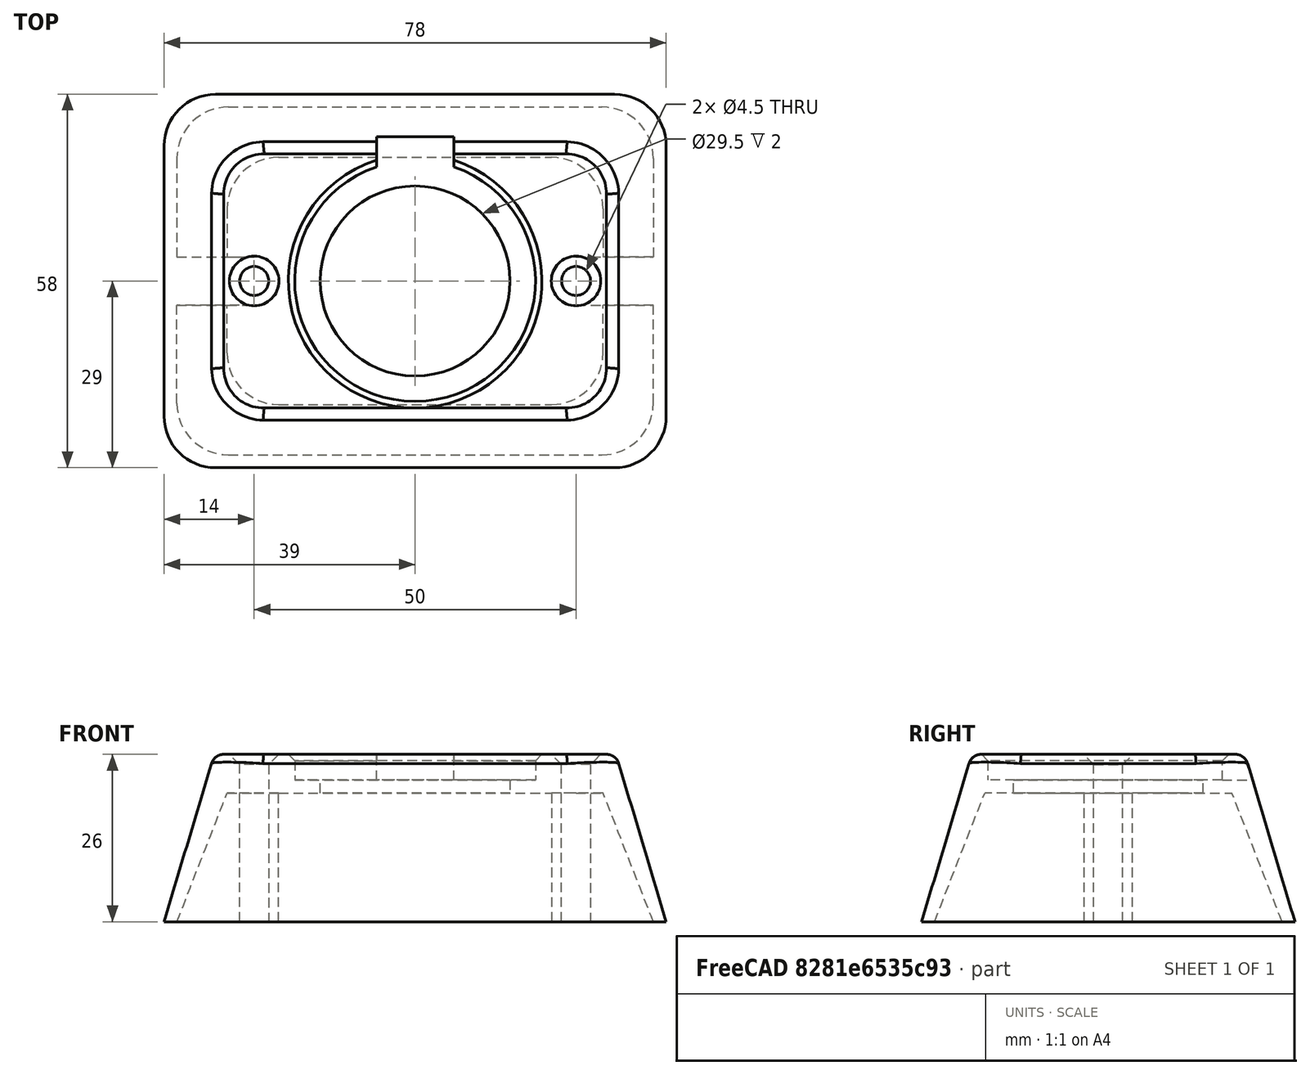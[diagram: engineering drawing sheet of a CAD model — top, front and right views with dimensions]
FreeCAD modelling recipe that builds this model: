
FCSTD DOCUMENT  (FreeCAD 0.20R29410 (Git))
Label: usb_spacer
License: All rights reserved
LicenseURL: http://en.wikipedia.org/wiki/All_rights_reserved
objects: Sketcher::SketchObject×6, PartDesign::Pocket×2, PartDesign::Chamfer×2, Spreadsheet::Sheet×1, PartDesign::AdditiveLoft×1, PartDesign::SubtractiveLoft×1, PartDesign::Fillet×1, PartDesign::Body×1, App::Part×1, Mesh::Feature×1
note: 21 computed .brp shape members not serialized (recipe doc carries the construction recipe); baked Part::Feature solids carry a one-line shape summary decoded from their .brp

FEATURE [Sketcher::SketchObject] Sketch  label="Sketch.Bottom"
  FullyConstrained = true
  MapMode = 5
  Support = -> [XY_Plane001]
  expr: Constraints[16] = <<Parameters>>.large_radius
  expr: Constraints[17] = <<Parameters>>.bottom_width
  expr: Constraints[3] = <<Parameters>>.bottom_length
  sketch-geometry (8):
    g0: LineSegment StartX=39 StartY=21 StartZ=0 EndX=39 EndY=-21 EndZ=0
    g1: LineSegment StartX=-39 StartY=-21 StartZ=0 EndX=-39 EndY=21 EndZ=0
    g2: ArcOfCircle CenterX=-31 CenterY=21 CenterZ=0 NormalX=0 NormalY=0 NormalZ=1 AngleXU=0 Radius=8 StartAngle=1.5708 EndAngle=3.14159
    g3: ArcOfCircle CenterX=31 CenterY=21 CenterZ=0 NormalX=0 NormalY=0 NormalZ=1 AngleXU=0 Radius=8 StartAngle=2e-16 EndAngle=1.5708
    g4: LineSegment StartX=-31 StartY=29 StartZ=0 EndX=31 EndY=29 EndZ=0
    g5: ArcOfCircle CenterX=-31 CenterY=-21 CenterZ=0 NormalX=0 NormalY=0 NormalZ=1 AngleXU=0 Radius=8 StartAngle=3.14159 EndAngle=4.71239
    g6: ArcOfCircle CenterX=31 CenterY=-21 CenterZ=0 NormalX=0 NormalY=0 NormalZ=1 AngleXU=0 Radius=8 StartAngle=4.71239 EndAngle=6.28319
    g7: LineSegment StartX=-31 StartY=-29 StartZ=0 EndX=31 EndY=-29 EndZ=0
  constraints (18):
    c: Vertical(g1)
    c: Symmetric(g1,g0,g-2)
    c: Symmetric(g0,g0,g-1)
    c: DistanceX(g1,g0) = 78
    c: Horizontal(g4)
    c: Horizontal(g7)
    c: Equal(g4,g7)
    c: Equal(g0,g1)
    c: Tangent(g4,g3) = 1.5708
    c: Tangent(g3,g0) = 1.5708
    c: Tangent(g4,g2) = 1.5708
    c: Tangent(g2,g1) = 1.5708
    c: Tangent(g5,g1) = 1.5708
    c: Tangent(g7,g5) = -1.5708
    c: Tangent(g7,g6) = -1.5708
    c: Tangent(g6,g0) = 1.5708
    c: Radius(g2) = 8
    c: DistanceY(g6,g3) = 58
FEATURE [Spreadsheet::Sheet] Spreadsheet  label="Parameters"
  cells = A1=Bottom; B2=bottom_length; C2(bottom_length)=78; B3=bottom_width; C3(bottom_width)=58; B4=bottom_wall; C4(bottom_wall)=2; A6=Top; B7=top_length; C7(top_length)==C2 - C13 * C18; D7=calc; B8=top_width; C8(top_width)==C3 - C13 * C18; D8=calc; B9=wall_taper_length; C9(wall_taper_length)==C2 - C13 * C18 - 2 * C4; D9=calc; B10=wall_taper_width; C10(wall_taper_width)==C3 - C13 * C18 - 2 * C4; D10=calc; A12=General; B13=height; C13(height)=26; B14=hole_diameter; C14(hole_diameter)=29.5; B15=face_thickness; C15(face)=6; B16=large_radius; C16(large_radius)=8; B17=small_radius; C17(small_radius)=2; B18=taper; C18=0.6; B19=flange_diameter; C19(flange_diameter)=37.4; B20=flange_depth; C20(flange_depth)=4; B21=cover_tab; C21(cover_tab)=12; A23=Screws; B24=screw_hole_diameter; C24(screw_hole_diameter)=4.5; B25=screw_seperation; C25(screw_seperation)=50; B26=post_diameter; C26(post_diameter)==C24 + 3; D26=calc; B27=screw_chamfer; C27(screw_chamfer)=1.6; A29=Switch; B30=switch_hole_diameter; C30(switch_hole_diameter)=6.1; B31=switch_offset; C31(switch_offset)=11
FEATURE [Sketcher::SketchObject] Sketch001  label="Sketch.Top"
  AttachmentOffset = pos=(0,0,26) rot=(0,0,1;0rad)
  FullyConstrained = true
  MapMode = 5
  Placement = pos=(0,0,26) rot=(0,0,1;0rad)
  Support = -> [XY_Plane001]
  expr: .AttachmentOffset.Base.z = <<Parameters>>.height
  expr: Constraints[15] = <<Parameters>>.top_width
  expr: Constraints[2] = <<Parameters>>.top_length
  expr: Constraints[3] = <<Parameters>>.large_radius
  sketch-geometry (8):
    g0: LineSegment StartX=31.2 StartY=13.2 StartZ=0 EndX=31.2 EndY=-13.2 EndZ=0
    g1: LineSegment StartX=-31.2 StartY=-13.2 StartZ=0 EndX=-31.2 EndY=13.2 EndZ=0
    g2: ArcOfCircle CenterX=-23.2 CenterY=-13.2 CenterZ=0 NormalX=0 NormalY=0 NormalZ=1 AngleXU=0 Radius=8 StartAngle=3.14159 EndAngle=4.71239
    g3: ArcOfCircle CenterX=23.2 CenterY=-13.2 CenterZ=0 NormalX=0 NormalY=0 NormalZ=1 AngleXU=0 Radius=8 StartAngle=4.71239 EndAngle=6.28319
    g4: LineSegment StartX=-23.2 StartY=-21.2 StartZ=0 EndX=23.2 EndY=-21.2 EndZ=0
    g5: ArcOfCircle CenterX=-23.2 CenterY=13.2 CenterZ=0 NormalX=0 NormalY=0 NormalZ=1 AngleXU=0 Radius=8 StartAngle=1.5708 EndAngle=3.14159
    g6: ArcOfCircle CenterX=23.2 CenterY=13.2 CenterZ=0 NormalX=0 NormalY=0 NormalZ=1 AngleXU=0 Radius=8 StartAngle=2e-16 EndAngle=1.5708
    g7: LineSegment StartX=-23.2 StartY=21.2 StartZ=0 EndX=23.2 EndY=21.2 EndZ=0
  constraints (16):
    c: Symmetric(g0,g0,g-1)
    c: Symmetric(g1,g0,g-2)
    c: DistanceX(g1,g0) = 62.4
    c: Radius(g5) = 8
    c: Symmetric(g5,g6,g-2)
    c: Tangent(g2,g1) = 1.5708
    c: Tangent(g4,g2) = -1.5708
    c: Tangent(g3,g0) = 1.5708
    c: Tangent(g4,g3) = -1.5708
    c: Tangent(g7,g6) = 1.5708
    c: Tangent(g6,g0) = 1.5708
    c: Tangent(g7,g5) = 1.5708
    c: Tangent(g5,g1) = 1.5708
    c: Symmetric(g2,g3,g-2)
    c: Equal(g4,g7)
    c: DistanceY(g3,g6) = 42.4
FEATURE [PartDesign::AdditiveLoft] AdditiveLoft  label="AdditiveLoft.Main"
  Closed = false
  Profile = -> Sketch
  Ruled = false
  Sections = -> [Sketch001]
FEATURE [Sketcher::SketchObject] Sketch002  label="Sketch.Holes"
  FullyConstrained = true
  MapMode = 5
  Support = -> [XY_Plane001]
  expr: Constraints[1] = <<Parameters>>.hole_diameter
  expr: Constraints[4] = <<Parameters>>.screw_seperation
  expr: Constraints[6] = <<Parameters>>.screw_hole_diameter
  sketch-geometry (3):
    g0: Circle CenterX=0 CenterY=0 CenterZ=0 NormalX=0 NormalY=0 NormalZ=1 AngleXU=0 Radius=14.75
    g1: Circle CenterX=-25 CenterY=0 CenterZ=0 NormalX=0 NormalY=0 NormalZ=1 AngleXU=0 Radius=2.25
    g2: Circle CenterX=25 CenterY=-1.76111e-11 CenterZ=0 NormalX=0 NormalY=0 NormalZ=1 AngleXU=0 Radius=2.25
  constraints (7):
    c: Coincident(g0,g-1)
    c: Diameter(g0) = 29.5
    c: PointOnObject(g1,g-1)
    c: Symmetric(g2,g1,g0)
    c: DistanceX(g1,g2) = 50
    c: Equal(g2,g1)
    c: Diameter(g2) = 4.5
FEATURE [PartDesign::Pocket] Pocket  label="Pocket.Screw"
  BaseFeature = -> AdditiveLoft
  Direction = (0,0,-1)
  Length = 78
  Length2 = 5
  Midplane = true
  Profile = -> Sketch002
  ReferenceAxis = -> Sketch002 [N_Axis]
  Type = 0
  expr: Length = <<Parameters>>.height * 3
FEATURE [Sketcher::SketchObject] Sketch003  label="Sketch.Interior.Bottom"
  FullyConstrained = true
  MapMode = 5
  Support = -> [XY_Plane001]
  expr: Constraints[15] = <<Parameters>>.post_diameter
  expr: Constraints[31] = <<Parameters>>.screw_seperation
  expr: Constraints[39] = <<Parameters>>.bottom_length - <<Parameters>>.bottom_wall * 2
  expr: Constraints[6] = <<Parameters>>.large_radius
  expr: Constraints[7] = <<Parameters>>.bottom_width - <<Parameters>>.bottom_wall * 2
  sketch-geometry (16):
    g0: ArcOfCircle CenterX=-29 CenterY=19 CenterZ=0 NormalX=0 NormalY=0 NormalZ=1 AngleXU=0 Radius=8 StartAngle=1.5708 EndAngle=3.14159
    g1: ArcOfCircle CenterX=29 CenterY=19 CenterZ=0 NormalX=0 NormalY=0 NormalZ=1 AngleXU=0 Radius=8 StartAngle=0 EndAngle=1.5708
    g2: ArcOfCircle CenterX=-29 CenterY=-19 CenterZ=0 NormalX=0 NormalY=0 NormalZ=1 AngleXU=0 Radius=8 StartAngle=3.14159 EndAngle=4.71239
    g3: ArcOfCircle CenterX=29 CenterY=-19 CenterZ=0 NormalX=0 NormalY=0 NormalZ=1 AngleXU=0 Radius=8 StartAngle=4.71239 EndAngle=6.28319
    g4: LineSegment StartX=-29 StartY=27 StartZ=0 EndX=29 EndY=27 EndZ=0
    g5: LineSegment StartX=-29 StartY=-27 StartZ=0 EndX=29 EndY=-27 EndZ=0
    g6: ArcOfCircle CenterX=-25 CenterY=0 CenterZ=0 NormalX=0 NormalY=0 NormalZ=1 AngleXU=0 Radius=3.75 StartAngle=4.71239 EndAngle=7.85398
    g7: LineSegment StartX=-37 StartY=19 StartZ=0 EndX=-37 EndY=3.75 EndZ=0
    g8: LineSegment StartX=-37 StartY=3.75 StartZ=0 EndX=-25 EndY=3.75 EndZ=0
    g9: LineSegment StartX=-25 StartY=-3.75 StartZ=0 EndX=-37 EndY=-3.75 EndZ=0
    g10: LineSegment StartX=-37 StartY=-19 StartZ=0 EndX=-37 EndY=-3.75 EndZ=0
    g11: ArcOfCircle CenterX=25 CenterY=0 CenterZ=0 NormalX=0 NormalY=0 NormalZ=1 AngleXU=0 Radius=3.75 StartAngle=1.5708 EndAngle=4.71239
    g12: LineSegment StartX=37 StartY=19 StartZ=0 EndX=37 EndY=3.75 EndZ=0
    g13: LineSegment StartX=37 StartY=-19 StartZ=0 EndX=37 EndY=-3.75 EndZ=0
    g14: LineSegment StartX=25 StartY=-3.75 StartZ=0 EndX=37 EndY=-3.75 EndZ=0
    g15: LineSegment StartX=25 StartY=3.75 StartZ=0 EndX=37 EndY=3.75 EndZ=0
  constraints (40):
    c: Horizontal(g5)
    c: Equal(g4,g5)
    c: Tangent(g4,g1) = 1.5708
    c: Tangent(g5,g3) = -1.5708
    c: Tangent(g5,g2) = -1.5708
    c: Tangent(g4,g0) = 1.5708
    c: Radius(g0) = 8
    c: DistanceY(g3,g1) = 54
    c: PointOnObject(g6,g-1)
    c: Vertical(g7)
    c: Coincident(g8,g7)
    c: Horizontal(g8)
    c: Horizontal(g9)
    c: Coincident(g10,g9)
    c: Vertical(g10)
    c: Diameter(g6) = 7.5
    c: Equal(g8,g9)
    c: Equal(g7,g10)
    c: Tangent(g8,g6) = 1.5708
    c: Tangent(g9,g6) = 1.5708
    c: Symmetric(g0,g1,g-2)
    c: Vertical(g12)
    c: Vertical(g13)
    c: Coincident(g14,g13)
    c: Horizontal(g14)
    c: Coincident(g15,g12)
    c: Horizontal(g15)
    c: Equal(g8,g15)
    c: Equal(g9,g14)
    c: Equal(g7,g12)
    c: Equal(g10,g13)
    c: DistanceX(g6,g11) = 50
    c: Tangent(g15,g11) = 1.5708
    c: Tangent(g14,g11) = -1.5708
    c: Symmetric(g6,g11,g-2)
    c: Tangent(g13,g3) = -1.5708
    c: Tangent(g12,g1) = 1.5708
    c: Tangent(g10,g2) = 1.5708
    c: Tangent(g7,g0) = -1.5708
    c: DistanceX(g2,g3) = 74
FEATURE [Sketcher::SketchObject] Sketch004  label="Sketch.Interior.Top"
  AttachmentOffset = pos=(0,0,20) rot=(0,0,1;0rad)
  FullyConstrained = true
  MapMode = 5
  Placement = pos=(0,0,20) rot=(0,0,1;0rad)
  Support = -> [XY_Plane001]
  expr: .AttachmentOffset.Base.z = <<Parameters>>.height - <<Parameters>>.face
  expr: Constraints[10] = <<Parameters>>.wall_taper_width
  expr: Constraints[12] = <<Parameters>>.post_diameter
  expr: Constraints[35] = <<Parameters>>.screw_seperation
  expr: Constraints[38] = <<Parameters>>.wall_taper_length
  expr: Constraints[6] = <<Parameters>>.large_radius
  sketch-geometry (16):
    g0: ArcOfCircle CenterX=-21.2 CenterY=11.2 CenterZ=0 NormalX=0 NormalY=0 NormalZ=1 AngleXU=0 Radius=8 StartAngle=1.5708 EndAngle=3.14159
    g1: ArcOfCircle CenterX=-21.2 CenterY=-11.2 CenterZ=0 NormalX=0 NormalY=0 NormalZ=1 AngleXU=0 Radius=8 StartAngle=3.14159 EndAngle=4.71239
    g2: ArcOfCircle CenterX=21.2 CenterY=-11.2 CenterZ=0 NormalX=0 NormalY=0 NormalZ=1 AngleXU=0 Radius=8 StartAngle=4.71239 EndAngle=6.28319
    g3: ArcOfCircle CenterX=21.2 CenterY=11.2 CenterZ=0 NormalX=0 NormalY=0 NormalZ=1 AngleXU=0 Radius=8 StartAngle=0 EndAngle=1.5708
    g4: LineSegment StartX=-21.2 StartY=19.2 StartZ=0 EndX=21.2 EndY=19.2 EndZ=0
    g5: LineSegment StartX=-21.2 StartY=-19.2 StartZ=0 EndX=21.2 EndY=-19.2 EndZ=0
    g6: ArcOfCircle CenterX=-25 CenterY=0 CenterZ=0 NormalX=0 NormalY=0 NormalZ=1 AngleXU=0 Radius=3.75 StartAngle=4.71239 EndAngle=7.85398
    g7: LineSegment StartX=-29.2 StartY=11.2 StartZ=0 EndX=-29.2 EndY=3.75 EndZ=0
    g8: LineSegment StartX=-29.2 StartY=3.75 StartZ=0 EndX=-25 EndY=3.75 EndZ=0
    g9: LineSegment StartX=-29.2 StartY=-11.2 StartZ=0 EndX=-29.2 EndY=-3.75 EndZ=0
    g10: LineSegment StartX=-29.2 StartY=-3.75 StartZ=0 EndX=-25 EndY=-3.75 EndZ=0
    g11: ArcOfCircle CenterX=25 CenterY=0 CenterZ=0 NormalX=0 NormalY=0 NormalZ=1 AngleXU=0 Radius=3.75 StartAngle=1.5708 EndAngle=4.71239
    g12: LineSegment StartX=25 StartY=3.75 StartZ=0 EndX=29.2 EndY=3.75 EndZ=0
    g13: LineSegment StartX=29.2 StartY=11.2 StartZ=0 EndX=29.2 EndY=3.75 EndZ=0
    g14: LineSegment StartX=29.2 StartY=-11.2 StartZ=0 EndX=29.2 EndY=-3.75 EndZ=0
    g15: LineSegment StartX=25 StartY=-3.75 StartZ=0 EndX=29.2 EndY=-3.75 EndZ=0
  constraints (40):
    c: Horizontal(g5)
    c: Horizontal(g4)
    c: Equal(g4,g5)
    c: Equal(g3,g0)
    c: Equal(g0,g1)
    c: Equal(g1,g2)
    c: Radius(g0) = 8
    c: Tangent(g4,g3) = 1.5708
    c: Tangent(g5,g2) = -1.5708
    c: Tangent(g5,g1) = -1.5708
    c: DistanceY(g2,g3) = 38.4
    c: PointOnObject(g6,g-1)
    c: Diameter(g6) = 7.5
    c: Vertical(g7)
    c: Coincident(g8,g7)
    c: Vertical(g9)
    c: Coincident(g10,g9)
    c: Horizontal(g10)
    c: Tangent(g8,g6) = 1.5708
    c: Tangent(g10,g6) = -1.5708
    c: Horizontal(g12)
    c: Coincident(g13,g12)
    c: Vertical(g13)
    c: Vertical(g14)
    c: Coincident(g15,g14)
    c: Horizontal(g15)
    c: Equal(g6,g11)
    c: Equal(g8,g12)
    c: Horizontal(g8)
    c: Tangent(g12,g11) = 1.5708
    c: Tangent(g15,g11) = -1.5708
    c: Tangent(g13,g3) = 1.5708
    c: Tangent(g14,g2) = -1.5708
    c: Tangent(g9,g1) = 1.5708
    c: Tangent(g7,g0) = -1.5708
    c: DistanceX(g6,g11) = 50
    c: Symmetric(g6,g11,g-2)
    c: Tangent(g4,g0) = 1.5708
    c: DistanceX(g1,g2) = 58.4
    c: Symmetric(g1,g0,g-1)
FEATURE [PartDesign::SubtractiveLoft] SubtractiveLoft  label="SubtractiveLoft.Interior"
  BaseFeature = -> Pocket
  Closed = false
  Profile = -> Sketch003
  Ruled = false
  Sections = -> [Sketch004]
FEATURE [Sketcher::SketchObject] Sketch005  label="Sketch.Flange"
  AttachmentOffset = pos=(0,0,22) rot=(0,0,1;0rad)
  FullyConstrained = true
  MapMode = 5
  Placement = pos=(0,0,22) rot=(0,0,1;0rad)
  Support = -> [XY_Plane001]
  expr: .AttachmentOffset.Base.z = <<Parameters>>.height - <<Parameters>>.flange_depth
  expr: Constraints[11] = <<Parameters>>.top_width / 3
  expr: Constraints[12] = <<Parameters>>.cover_tab
  expr: Constraints[7] = <<Parameters>>.flange_diameter
  sketch-geometry (4):
    g0: ArcOfCircle CenterX=0 CenterY=0 CenterZ=0 NormalX=0 NormalY=0 NormalZ=1 AngleXU=0 Radius=18.7 StartAngle=1.89743 EndAngle=7.52735
    g1: LineSegment StartX=-6 StartY=17.7113 StartZ=0 EndX=-6 EndY=31.8446 EndZ=0
    g2: LineSegment StartX=-6 StartY=31.8446 StartZ=0 EndX=6 EndY=31.8446 EndZ=0
    g3: LineSegment StartX=6 StartY=17.7113 StartZ=0 EndX=6 EndY=31.8446 EndZ=0
  constraints (13):
    c: Coincident(g0,g-1)
    c: Coincident(g1,g0)
    c: Vertical(g1)
    c: Coincident(g2,g1)
    c: Horizontal(g2)
    c: Coincident(g3,g0)
    c: Coincident(g3,g2)
    c: Diameter(g0) = 37.4
    c: Symmetric(g0,g0,g-2)
    c: Vertical(g3)
    c: Equal(g1,g3)
    c: DistanceY(g3,g3) = 14.1333
    c: DistanceX(g2,g2) = 12
FEATURE [PartDesign::Pocket] Pocket001  label="Pocket.Flange"
  BaseFeature = -> SubtractiveLoft
  Direction = (0,0,-1)
  Length = 5
  Length2 = 5
  Profile = -> Sketch005
  ReferenceAxis = -> Sketch005 [N_Axis]
  Reversed = true
  Type = 0
FEATURE [PartDesign::Fillet] Fillet  label="Fillet.Outer"
  Base = -> Pocket001 [Edge46]
  BaseFeature = -> Pocket001
  Radius = 2
  SupportTransform = false
  UseAllEdges = false
  expr: Radius = <<Parameters>>.small_radius
FEATURE [PartDesign::Chamfer] Chamfer  label="Chamfer.Screws"
  Angle = 45
  Base = -> Fillet [Edge64,Edge63]
  BaseFeature = -> Fillet
  ChamferType = 0
  FlipDirection = false
  Size = 1.6
  Size2 = 1
  SupportTransform = false
  UseAllEdges = false
  expr: Size = <<Parameters>>.screw_chamfer
FEATURE [PartDesign::Chamfer] Chamfer001  label="Chamfer.Flange"
  Angle = 45
  Base = -> Chamfer [Edge4]
  BaseFeature = -> Chamfer
  ChamferType = 0
  FlipDirection = false
  Size = 1
  Size2 = 1
  SupportTransform = false
  UseAllEdges = false
FEATURE [PartDesign::Body] Body
  Group = -> [Sketch,Sketch001,AdditiveLoft,Sketch002,Pocket,Sketch003,Sketch004,SubtractiveLoft,Sketch005,Pocket001,Fillet,Chamfer,Chamfer001]
  Origin = -> Origin001
  Tip = -> Chamfer001
FEATURE [App::Part] Part
  Group = -> [Body]
  Origin = -> Origin
FEATURE [Mesh::Feature] Mesh  label="Body (Meshed)"
